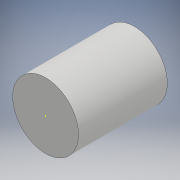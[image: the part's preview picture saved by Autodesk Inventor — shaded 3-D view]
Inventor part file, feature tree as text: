
AUTODESK INVENTOR PART (.ipt)
format: ipt  version: 2018 (Build 220112000, 112)  size: 102,400 bytes
history: native  units: mm
features: sketch x3, extrude x2
ambient origin geometry x8: Origin, YZ Plane, XZ Plane, XY Plane, X Axis, Y Axis, Z Axis, Center Point
bodies: Solide1 (feature_tree)
feature tree (5):
  sketch  "Esquisse1"
  extrude  "Extrusion1"  Depth=20.0mm
  extrude  "Extrusion2"  Depth=2.0mm TaperAngle=0.0deg
  sketch  "Esquisse2"
  sketch  "Esquisse3"
